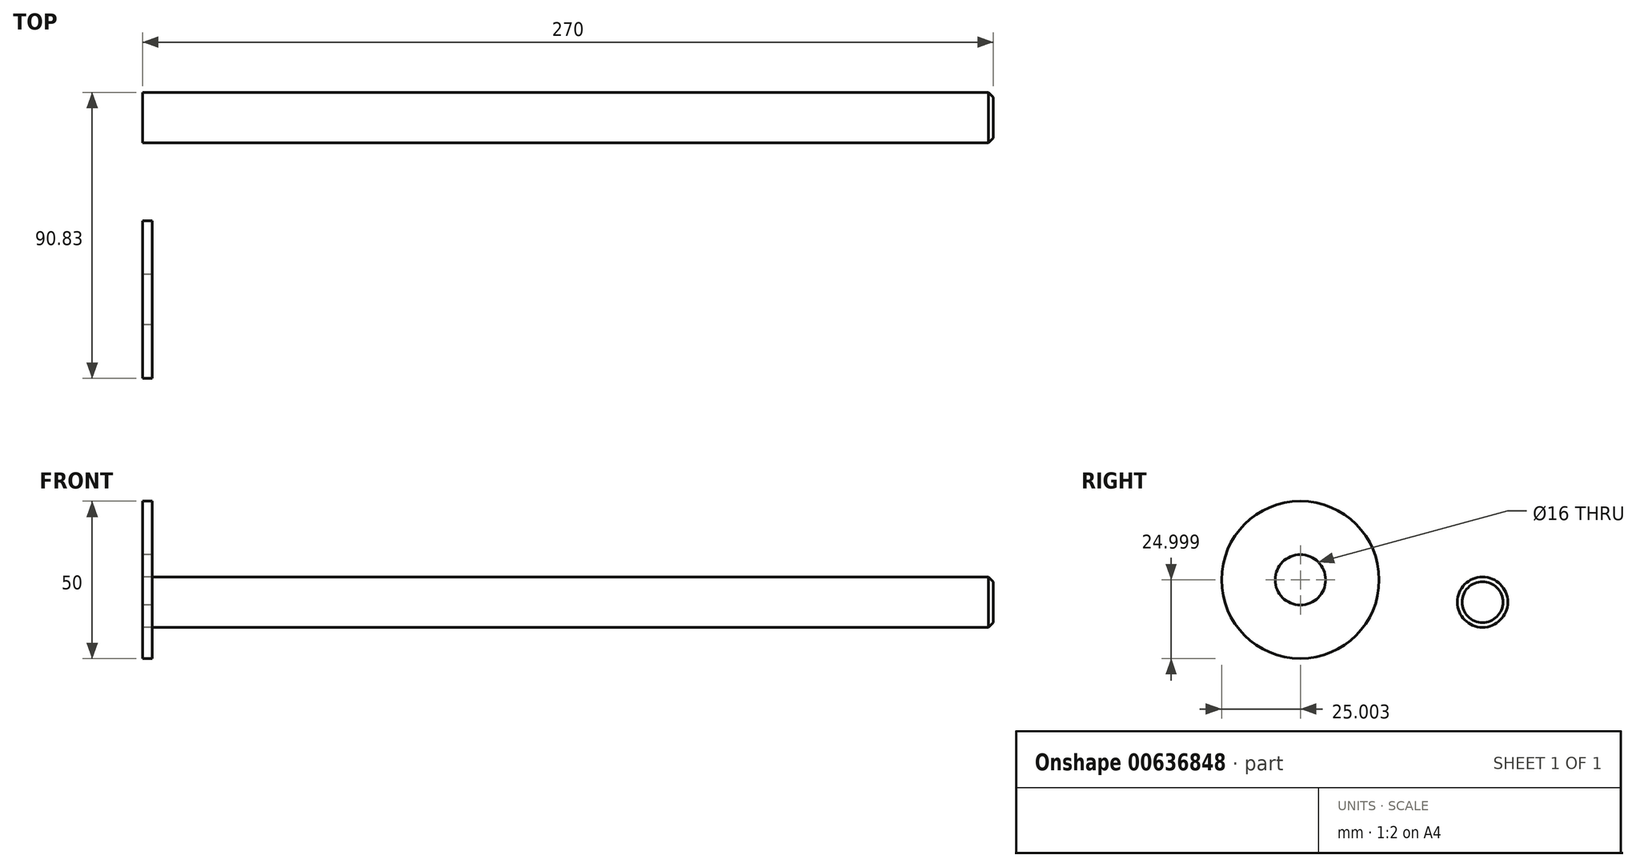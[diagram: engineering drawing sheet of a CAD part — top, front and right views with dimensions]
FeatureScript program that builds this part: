
annotation { "Feature Type Name" : "Feature", "Feature Type Description" : "" }
export const myFeature = defineFeature(function(context is Context, id is Id, definition is map)
    precondition{}
    {
        {
            var Q0;
            Q0=qCreatedBy(makeId("Right.planeOp"),FACE);
            var sketch = newSketch(context, id + "F0", { "sketchPlane" : qUnion([Q0])});
            skCircle(sketch, "E0", {"center": v(0, 0) * mm, "radius": 8 * mm});
            skSolve(sketch);
        }
        {
            var Q0;
            Q0=makeQuery(id+"F0.imprint","IMPRINT",FACE,{"disambiguationData":[TD([[makeQuery(id+"F0.imprint","IMPRINT",EDGE,{"derivedFrom":sQuery(id+"F0.wireOp",EDGE,"E0")}),1.0]])]});
            extrude(context, id + "F1", {"entities" : qUnion([Q0]), "depth" : 270 * mm, "offsetDistance" : 25 * mm});
        }
        {
            var Q0;
            Q0=makeQuery(id+"F1.opExtrude","CAP_FACE",FACE,{"disambiguationData":[OSD([sQuery(id+"F0.wireOp",EDGE,"E0")])],"isStart":false});
            chamfer(context, id + "F2", {"entities" : qUnion([Q0]), "width" : 1.5 * mm, "tangentPropagation" : true});
        }
        {
            var Q0;
            Q0=qCreatedBy(makeId("Right.planeOp"),FACE);
            var sketch = newSketch(context, id + "F3", { "sketchPlane" : qUnion([Q0])});
            skCircle(sketch, "E1", {"center": v(-57.83, 7.09) * mm, "radius": 25 * mm});
            skCircle(sketch, "E2", {"center": v(-57.83, 7.09) * mm, "radius": 8 * mm});
            skSolve(sketch);
        }
        {
            var Q0;
            Q0=makeQuery(id+"F3.imprint","IMPRINT",FACE,{"disambiguationData":[TD([[makeQuery(id+"F3.imprint","IMPRINT",EDGE,{"derivedFrom":sQuery(id+"F3.wireOp",EDGE,"E1")}),1.0]])]});
            extrude(context, id + "F4", {"entities" : qUnion([Q0]), "depth" : 3 * mm, "offsetDistance" : 25 * mm});
        }
    });
